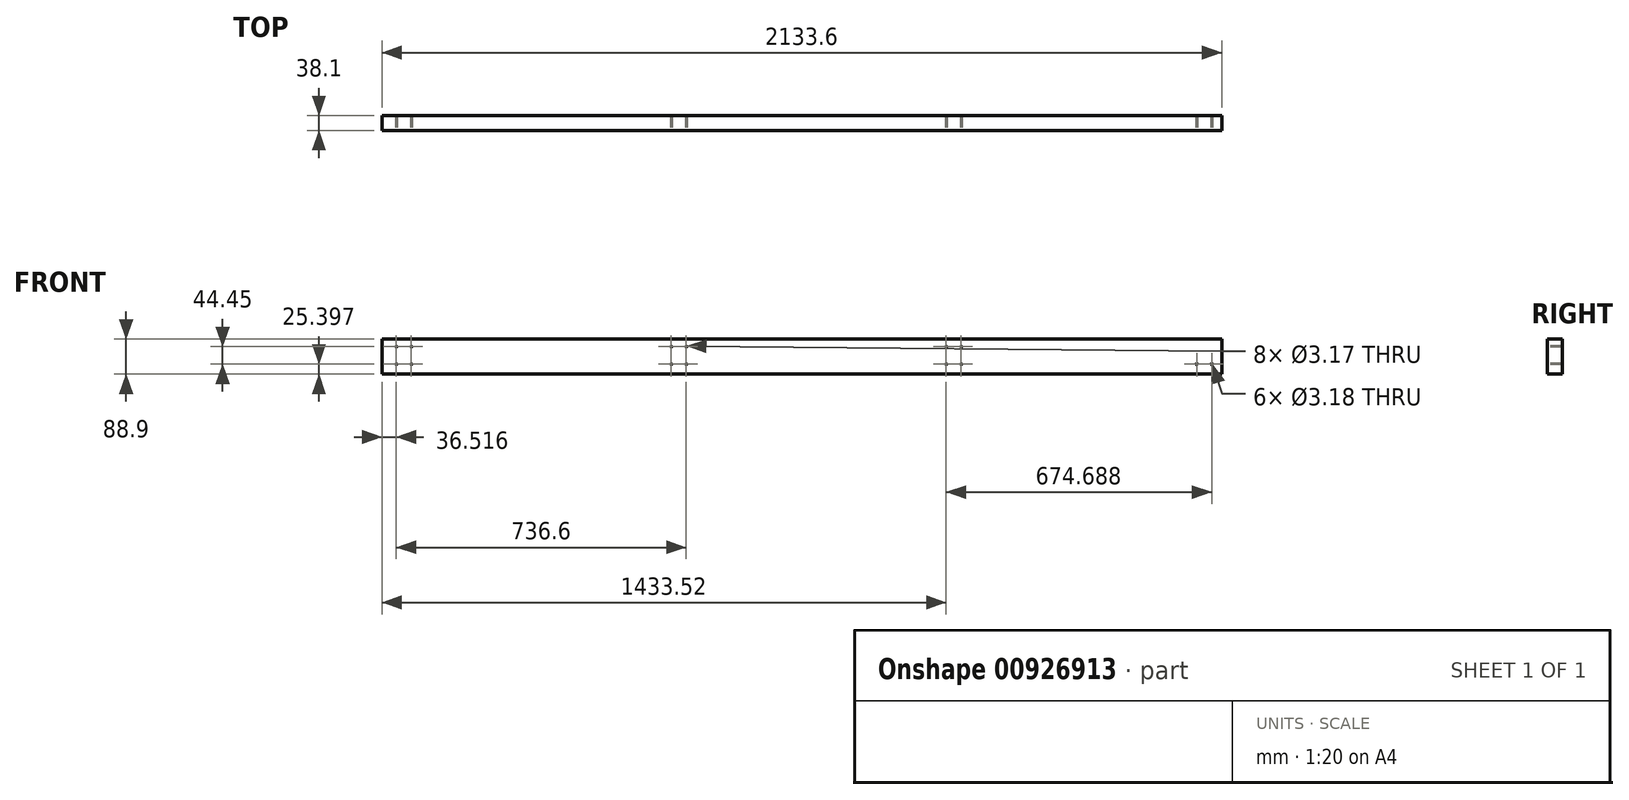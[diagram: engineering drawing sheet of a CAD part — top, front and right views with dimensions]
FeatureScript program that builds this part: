
annotation { "Feature Type Name" : "Feature", "Feature Type Description" : "" }
export const myFeature = defineFeature(function(context is Context, id is Id, definition is map)
    precondition{}
    {
        {
            var Q0;
            Q0=qCreatedBy(makeId("Front.planeOp"),FACE);
            var sketch = newSketch(context, id + "F0", { "sketchPlane" : qUnion([Q0])});
            skLineSegment(sketch, "E0.bottom", {"start": v(-112.7, 108.74) * mm, "end": v(2020.9, 108.74) * mm});
            skLineSegment(sketch, "E0.top", {"start": v(-112.7, 19.84) * mm, "end": v(2020.9, 19.84) * mm});
            skLineSegment(sketch, "E0.left", {"start": v(-112.7, 108.74) * mm, "end": v(-112.7, 19.84) * mm});
            skLineSegment(sketch, "E0.right", {"start": v(2020.9, 108.74) * mm, "end": v(2020.9, 19.84) * mm});
            skSolve(sketch);
        }
        {
            var Q0;
            Q0=makeQuery(id+"F0.imprint","IMPRINT",FACE,{"disambiguationData":[TD([[makeQuery(id+"F0.imprint","IMPRINT",EDGE,{"derivedFrom":sQuery(id+"F0.wireOp",EDGE,"E0.bottom")}),-1.0]])]});
            extrude(context, id + "F1", {"entities" : qUnion([Q0]), "depth" : 38.1 * mm, "offsetDistance" : 25.4 * mm});
        }
        {
            var Q0;
            Q0=makeQuery(id+"F1.opExtrude","CAP_FACE",FACE,{"disambiguationData":[OSD([sQuery(id+"F0.wireOp",EDGE,"E0.bottom"),sQuery(id+"F0.wireOp",EDGE,"E0.top"),sQuery(id+"F0.wireOp",EDGE,"E0.left"),sQuery(id+"F0.wireOp",EDGE,"E0.right")])],"isStart":false});
            var sketch = newSketch(context, id + "F2", { "sketchPlane" : qUnion([Q0])});
            skLineSegment(sketch, "E1", {"start": v(-112.7, 89.69) * mm, "end": v(-73.74, 89.69) * mm, "construction": true});
            skLineSegment(sketch, "E2", {"start": v(-112.7, 45.24) * mm, "end": v(-74.77, 45.24) * mm, "construction": true});
            skPoint(sketch, "E3", {"position": v(-76.2, 89.69) * mm});
            skPoint(sketch, "E4", {"position": v(-38.1, 89.69) * mm});
            skPoint(sketch, "E5", {"position": v(-76.18, 45.24) * mm});
            skPoint(sketch, "E6", {"position": v(-38.08, 45.24) * mm});
            skLineSegment(sketch, "E7", {"start": v(292.1, 19.84) * mm, "end": v(292.1, 108.74) * mm, "construction": true});
            skPoint(sketch, "E8.MirrorP", {"position": v(622.3, 45.24) * mm});
            skPoint(sketch, "E9.MirrorP", {"position": v(660.4, 45.24) * mm});
            skPoint(sketch, "E10.MirrorP", {"position": v(660.4, 89.69) * mm});
            skPoint(sketch, "E11.MirrorP", {"position": v(622.3, 89.69) * mm});
            skLineSegment(sketch, "E12", {"start": v(-101.6, 19.84) * mm, "end": v(-101.6, 108.74) * mm, "construction": true});
            skLineSegment(sketch, "E13", {"start": v(-12.7, 19.84) * mm, "end": v(-12.7, 108.74) * mm, "construction": true});
            skLineSegment(sketch, "E14", {"start": v(685.8, 19.84) * mm, "end": v(685.8, 108.74) * mm, "construction": true});
            skLineSegment(sketch, "E15", {"start": v(990.6, 19.84) * mm, "end": v(990.6, 108.74) * mm, "construction": true});
            skPoint(sketch, "E16.MirrorP", {"position": v(1358.92, 45.24) * mm});
            skPoint(sketch, "E17.MirrorP", {"position": v(1320.82, 45.24) * mm});
            skPoint(sketch, "E18.MirrorP", {"position": v(1320.8, 89.69) * mm});
            skPoint(sketch, "E19.MirrorP", {"position": v(1358.9, 89.69) * mm});
            skPoint(sketch, "E20", {"position": v(1957.4, 45.24) * mm});
            skPoint(sketch, "E21", {"position": v(1995.5, 45.24) * mm});
            skSolve(sketch);
        }
        {
            var Q0;
            Q0=sQuery(id+"F2.wireOp",VERTEX,"E21");
            var Q1;
            Q1=sQuery(id+"F2.wireOp",VERTEX,"E20");
            var Q2;
            Q2=sQuery(id+"F2.wireOp",VERTEX,"E19.MirrorP");
            var Q3;
            Q3=sQuery(id+"F2.wireOp",VERTEX,"E16.MirrorP");
            var Q4;
            Q4=sQuery(id+"F2.wireOp",VERTEX,"E17.MirrorP");
            var Q5;
            Q5=sQuery(id+"F2.wireOp",VERTEX,"E18.MirrorP");
            var Q6;
            Q6=sQuery(id+"F2.wireOp",VERTEX,"E9.MirrorP");
            var Q7;
            Q7=sQuery(id+"F2.wireOp",VERTEX,"E8.MirrorP");
            var Q8;
            Q8=sQuery(id+"F2.wireOp",VERTEX,"E11.MirrorP");
            var Q9;
            Q9=sQuery(id+"F2.wireOp",VERTEX,"E10.MirrorP");
            var Q10;
            Q10=sQuery(id+"F2.wireOp",VERTEX,"E5");
            var Q11;
            Q11=sQuery(id+"F2.wireOp",VERTEX,"E6");
            var Q12;
            Q12=sQuery(id+"F2.wireOp",VERTEX,"E4");
            var Q13;
            Q13=sQuery(id+"F2.wireOp",VERTEX,"E3");
            var Q14;
            Q14=makeQuery(id+"F1.opExtrude","SWEPT_BODY",BODY,{"disambiguationData":[OSD([sQuery(id+"F0.wireOp",EDGE,"E0.bottom"),sQuery(id+"F0.wireOp",EDGE,"E0.top"),sQuery(id+"F0.wireOp",EDGE,"E0.left"),sQuery(id+"F0.wireOp",EDGE,"E0.right")])]});
            hole(context, id + "F3", {"style" : HoleStyle.SIMPLE, "endStyle" : HoleEndStyle.THROUGH, "holeDiameter" : 3.17 * mm, "majorDiameter" : 6.35 * mm, "isTappedThrough" : true, "tappedDepth" : 12.7 * mm, "tapClearance" : 3, "locations" : qUnion([Q0, Q1, Q2, Q3, Q4, Q5, Q6, Q7, Q8, Q9, Q10, Q11, Q12, Q13]), "scope" : qUnion([Q14])});
        }
    });
